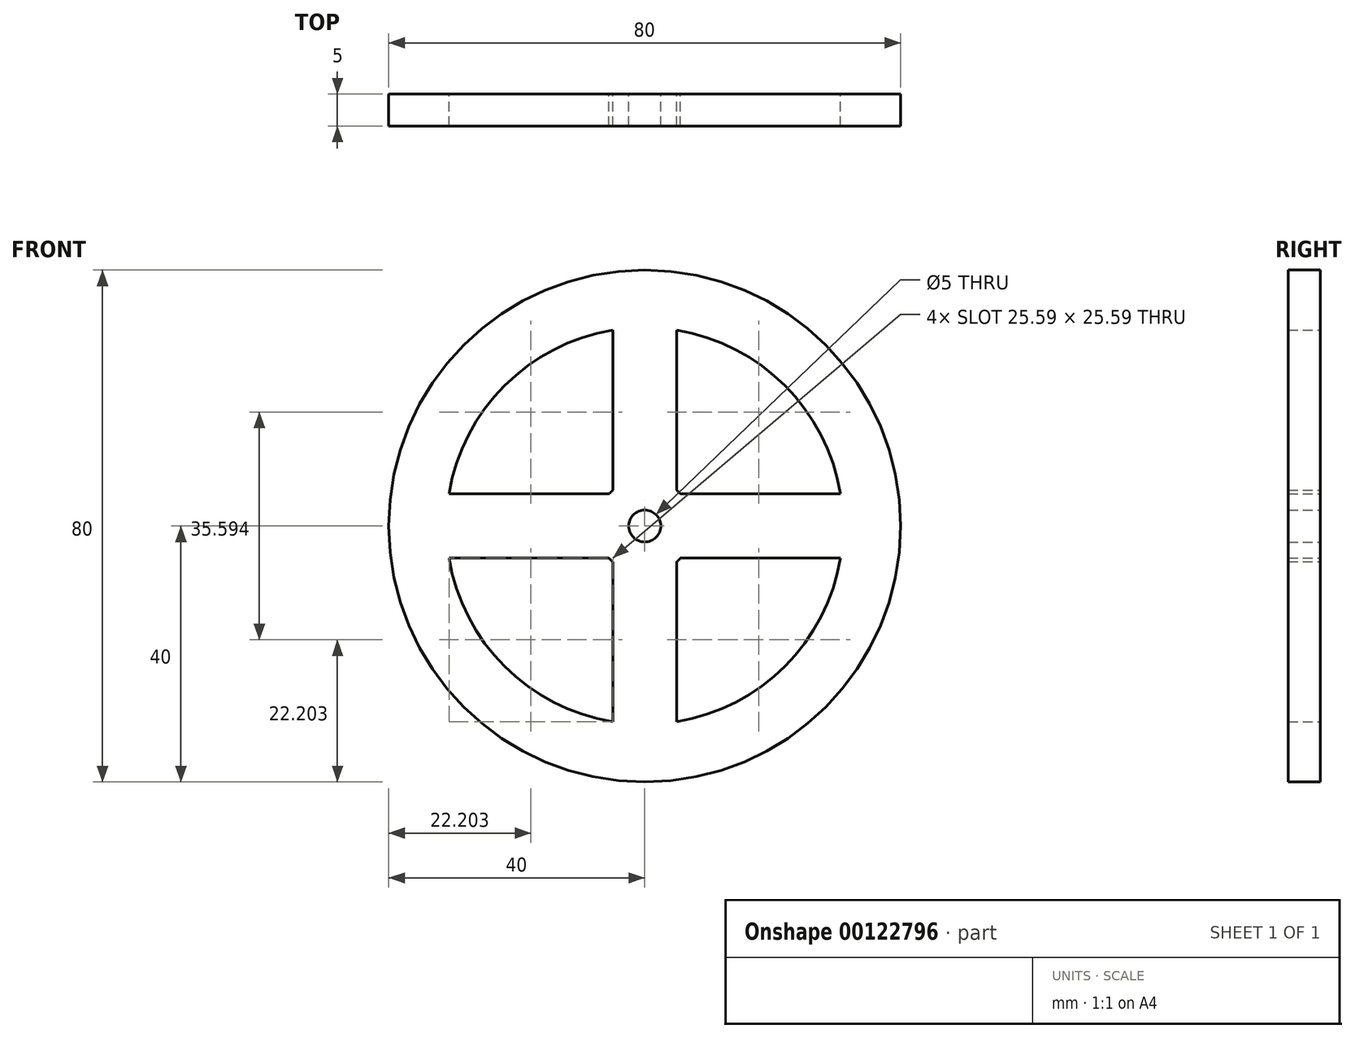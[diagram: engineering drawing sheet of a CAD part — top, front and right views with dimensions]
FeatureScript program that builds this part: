
annotation { "Feature Type Name" : "Feature", "Feature Type Description" : "" }
export const myFeature = defineFeature(function(context is Context, id is Id, definition is map)
    precondition{}
    {
        {
            var Q0;
            Q0=qCreatedBy(makeId("Front.planeOp"),FACE);
            var sketch = newSketch(context, id + "F0", { "sketchPlane" : qUnion([Q0])});
            skCircle(sketch, "E0", {"center": v(0, 0) * mm, "radius": 40 * mm});
            skArc(sketch, "E1", {"start": v(-5, 30.6) * mm, "mid": v(-21.92, 21.92) * mm, "end": v(-30.6, 5) * mm});
            skArc(sketch, "E2", {"start": v(-5, 5.6) * mm, "mid": v(-5.3, 5.3) * mm, "end": v(-5.6, 5) * mm});
            skCircle(sketch, "E3", {"center": v(0, 0) * mm, "radius": 2.5 * mm});
            skLineSegment(sketch, "E4", {"start": v(0, 2.5) * mm, "end": v(0, 31) * mm, "construction": true});
            skLineSegment(sketch, "E5", {"start": v(2.5, 0) * mm, "end": v(31, 0) * mm, "construction": true});
            skLineSegment(sketch, "E6", {"start": v(0, -7.5) * mm, "end": v(0, -31) * mm, "construction": true});
            skLineSegment(sketch, "E7", {"start": v(-7.5, 0) * mm, "end": v(-31, 0) * mm, "construction": true});
            skLineSegment(sketch, "E8.0", {"start": v(-5, 5.6) * mm, "end": v(-5, 30.6) * mm});
            skLineSegment(sketch, "E9.0", {"start": v(5, 5.6) * mm, "end": v(5, 30.6) * mm});
            skLineSegment(sketch, "E10.0", {"start": v(-5.6, 5) * mm, "end": v(-30.6, 5) * mm});
            skLineSegment(sketch, "E11.0", {"start": v(-5.6, -5) * mm, "end": v(-30.6, -5) * mm});
            skLineSegment(sketch, "E12.0", {"start": v(-5, -5.6) * mm, "end": v(-5, -30.6) * mm});
            skLineSegment(sketch, "E13.0", {"start": v(5, -5.6) * mm, "end": v(5, -30.6) * mm});
            skLineSegment(sketch, "E14.0", {"start": v(5.6, -5) * mm, "end": v(30.6, -5) * mm});
            skLineSegment(sketch, "E15.0", {"start": v(5.6, 5) * mm, "end": v(30.6, 5) * mm});
            skArc(sketch, "E16.trimOffspring", {"start": v(30.6, 5) * mm, "mid": v(21.92, 21.92) * mm, "end": v(5, 30.6) * mm});
            skArc(sketch, "E17.trimOffspring", {"start": v(5, -30.6) * mm, "mid": v(21.92, -21.92) * mm, "end": v(30.6, -5) * mm});
            skArc(sketch, "E18.trimOffspring", {"start": v(-30.6, -5) * mm, "mid": v(-21.92, -21.92) * mm, "end": v(-5, -30.6) * mm});
            skArc(sketch, "E19.trimOffspring", {"start": v(5.6, 5) * mm, "mid": v(5.3, 5.3) * mm, "end": v(5, 5.6) * mm});
            skArc(sketch, "E20.trimOffspring", {"start": v(5, -5.6) * mm, "mid": v(5.3, -5.3) * mm, "end": v(5.6, -5) * mm});
            skArc(sketch, "E21.trimOffspring", {"start": v(-5.6, -5) * mm, "mid": v(-5.3, -5.3) * mm, "end": v(-5, -5.6) * mm});
            skLineSegment(sketch, "E22", {"start": v(-7.5, 0) * mm, "end": v(-2.5, 0) * mm, "construction": true});
            skSolve(sketch);
        }
        {
            var Q0;
            Q0=makeQuery(id+"F0.imprint","IMPRINT",FACE,{"disambiguationData":[TD([[makeQuery(id+"F0.imprint","IMPRINT",EDGE,{"derivedFrom":sQuery(id+"F0.wireOp",EDGE,"E0")}),1.0]])]});
            var Q1;
            Q1=sQuery(id+"F0.wireOp",EDGE,"E4");
            var Q2;
            Q2=sQuery(id+"F0.wireOp",EDGE,"E5");
            var Q3;
            Q3=sQuery(id+"F0.wireOp",EDGE,"E6");
            var Q4;
            Q4=sQuery(id+"F0.wireOp",EDGE,"E7");
            var Q5;
            Q5=sQuery(id+"F0.wireOp",EDGE,"E22");
            extrude(context, id + "F1", {"entities" : qUnion([Q0]), "surfaceEntities" : qUnion([Q1, Q2, Q3, Q4, Q5]), "endBound" : BoundingType.SYMMETRIC, "depth" : 5 * mm});
        }
    });
